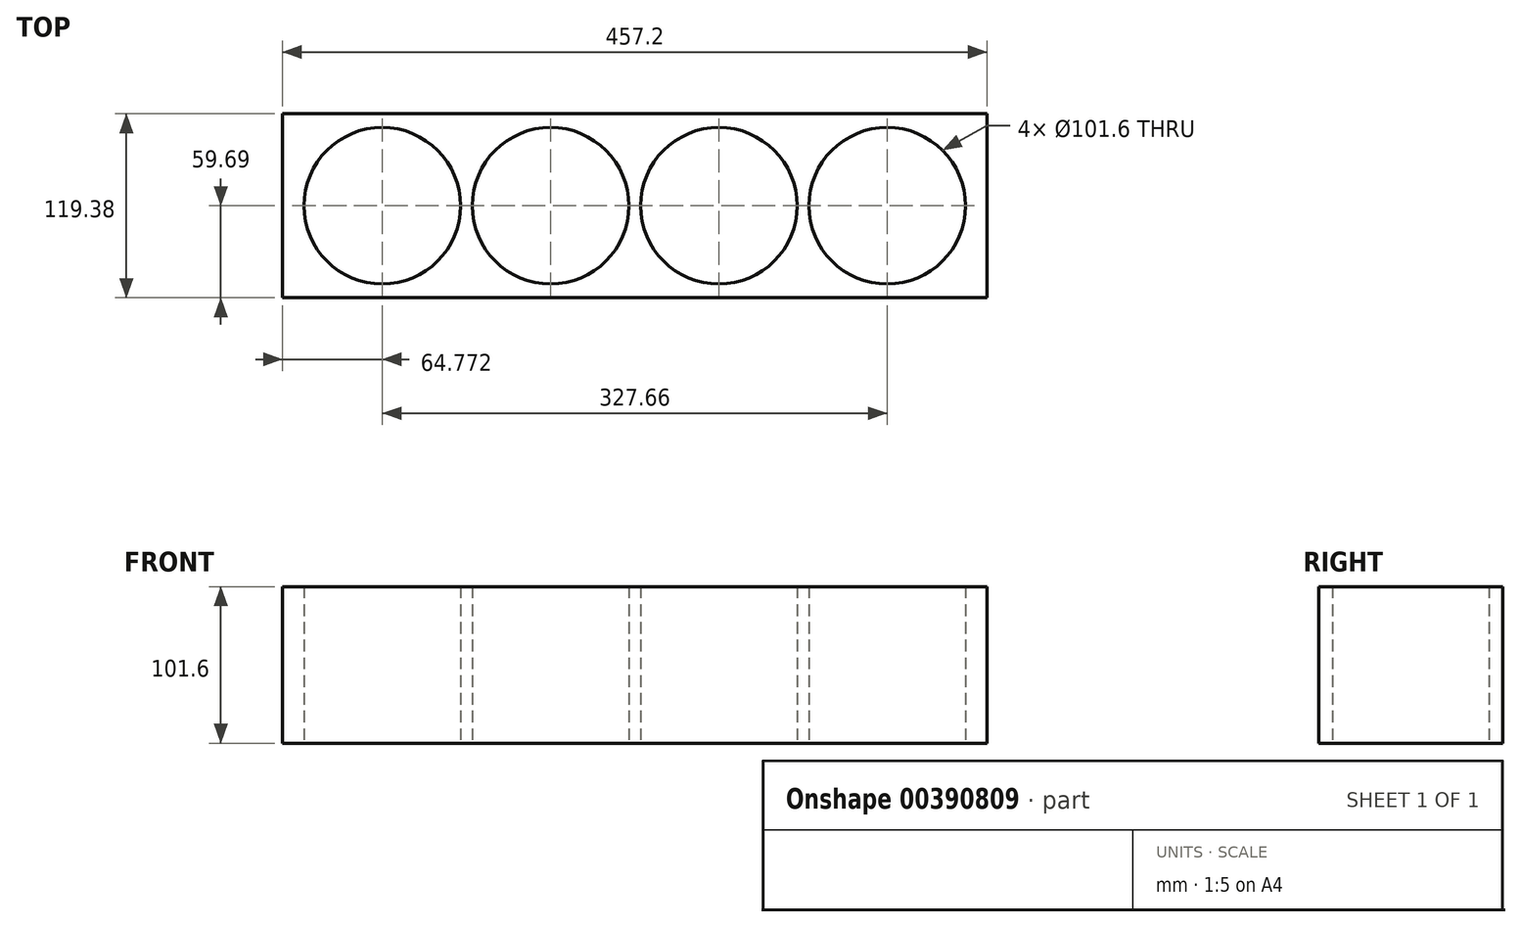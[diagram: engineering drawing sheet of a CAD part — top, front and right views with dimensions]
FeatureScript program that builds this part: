
annotation { "Feature Type Name" : "Feature", "Feature Type Description" : "" }
export const myFeature = defineFeature(function(context is Context, id is Id, definition is map)
    precondition{}
    {
        {
            var Q0;
            Q0=qCreatedBy(makeId("Top.planeOp"),FACE);
            var sketch = newSketch(context, id + "F0", { "sketchPlane" : qUnion([Q0])});
            skCircle(sketch, "E0", {"center": v(-321.93, 0) * mm, "radius": 50.8 * mm});
            skCircle(sketch, "E1.1.0.0", {"center": v(-212.7, 0) * mm, "radius": 50.8 * mm});
            skCircle(sketch, "E1.2.0.0", {"center": v(-103.49, 0) * mm, "radius": 50.8 * mm});
            skCircle(sketch, "E1.3.0.0", {"center": v(5.73, 0) * mm, "radius": 50.8 * mm});
            skLineSegment(sketch, "E2", {"start": v(-321.93, 0) * mm, "end": v(5.73, 0) * mm, "construction": true});
            skLineSegment(sketch, "E3.bottom", {"start": v(70.5, 59.69) * mm, "end": v(-386.7, 59.69) * mm});
            skLineSegment(sketch, "E3.top", {"start": v(70.5, -59.7) * mm, "end": v(-386.7, -59.7) * mm});
            skLineSegment(sketch, "E3.left", {"start": v(70.5, 59.69) * mm, "end": v(70.5, -59.7) * mm});
            skLineSegment(sketch, "E3.right", {"start": v(-386.7, 59.69) * mm, "end": v(-386.7, -59.7) * mm});
            skPoint(sketch, "E3.middle", {"position": v(-158.1, 0) * mm});
            skSolve(sketch);
        }
        {
            var Q0;
            Q0=makeQuery(id+"F0.imprint","IMPRINT",FACE,{"disambiguationData":[TD([[makeQuery(id+"F0.imprint","IMPRINT",EDGE,{"derivedFrom":sQuery(id+"F0.wireOp",EDGE,"E0")}),-1.0]])]});
            extrude(context, id + "F1", {"entities" : qUnion([Q0]), "depth" : 101.6 * mm, "offsetDistance" : 25.4 * mm});
        }
    });
